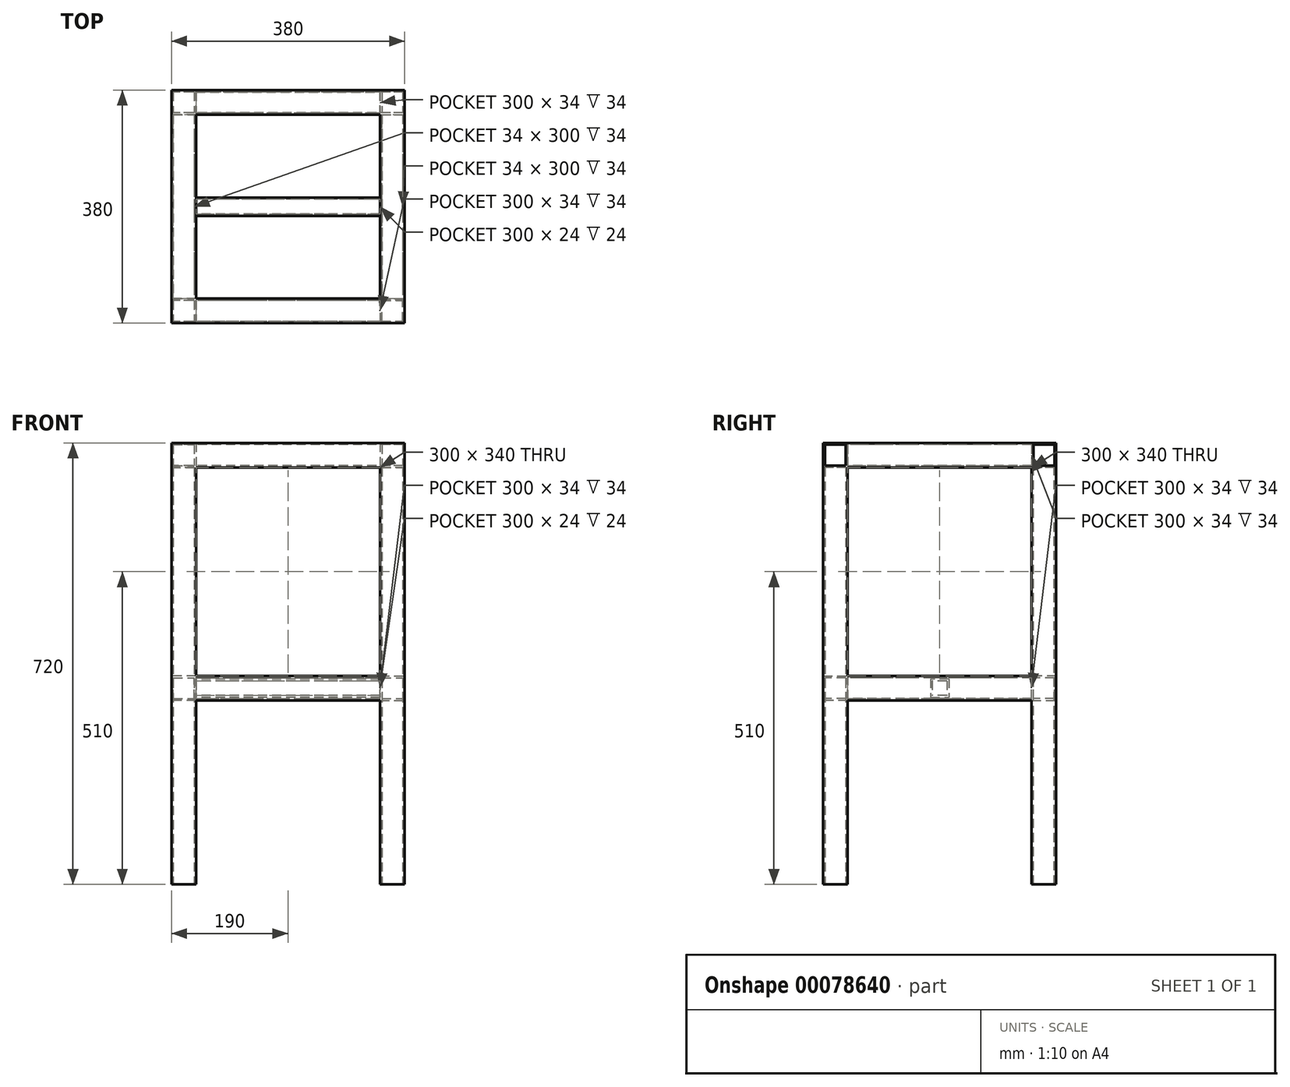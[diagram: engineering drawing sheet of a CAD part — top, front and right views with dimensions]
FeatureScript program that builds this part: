
annotation { "Feature Type Name" : "Feature", "Feature Type Description" : "" }
export const myFeature = defineFeature(function(context is Context, id is Id, definition is map)
    precondition{}
    {
        {
            var Q0;
            Q0=qCreatedBy(makeId("Top.planeOp"),FACE);
            var sketch = newSketch(context, id + "F0", { "sketchPlane" : qUnion([Q0])});
            skLineSegment(sketch, "E0.bottom", {"start": v(0, 0) * mm, "end": v(-40, 0) * mm});
            skLineSegment(sketch, "E0.top", {"start": v(0, -40) * mm, "end": v(-40, -40) * mm});
            skLineSegment(sketch, "E0.left", {"start": v(0, 0) * mm, "end": v(0, -40) * mm});
            skLineSegment(sketch, "E0.right", {"start": v(-40, 0) * mm, "end": v(-40, -40) * mm});
            skLineSegment(sketch, "E1.bottom", {"start": v(-3, -3) * mm, "end": v(-37, -3) * mm});
            skLineSegment(sketch, "E1.top", {"start": v(-3, -37) * mm, "end": v(-37, -37) * mm});
            skLineSegment(sketch, "E1.left", {"start": v(-3, -3) * mm, "end": v(-3, -37) * mm});
            skLineSegment(sketch, "E1.right", {"start": v(-37, -3) * mm, "end": v(-37, -37) * mm});
            skSolve(sketch);
        }
        {
            var Q0;
            Q0=makeQuery(id+"F0.imprint","IMPRINT",FACE,{"disambiguationData":[TD([[makeQuery(id+"F0.imprint","IMPRINT",EDGE,{"derivedFrom":sQuery(id+"F0.wireOp",EDGE,"E0.bottom")}),1.0]])]});
            extrude(context, id + "F1", {"entities" : qUnion([Q0]), "depth" : 380 * mm});
        }
        {
            var Q0;
            Q0=makeQuery(id+"F1.opExtrude","SWEPT_FACE",FACE,{"disambiguationData":[OSD([sQuery(id+"F0.wireOp",EDGE,"E0.left")])]});
            var sketch = newSketch(context, id + "F2", { "sketchPlane" : qUnion([Q0])});
            skLineSegment(sketch, "E2.bottom", {"start": v(-40, 0) * mm, "end": v(0, 0) * mm});
            skLineSegment(sketch, "E2.top", {"start": v(-40, 40) * mm, "end": v(0, 40) * mm});
            skLineSegment(sketch, "E2.left", {"start": v(-40, 0) * mm, "end": v(-40, 40) * mm});
            skLineSegment(sketch, "E2.right", {"start": v(0, 0) * mm, "end": v(0, 40) * mm});
            skLineSegment(sketch, "E3.bottom", {"start": v(-3, 37) * mm, "end": v(-37, 37) * mm});
            skLineSegment(sketch, "E3.top", {"start": v(-3, 3) * mm, "end": v(-37, 3) * mm});
            skLineSegment(sketch, "E3.left", {"start": v(-3, 37) * mm, "end": v(-3, 3) * mm});
            skLineSegment(sketch, "E3.right", {"start": v(-37, 37) * mm, "end": v(-37, 3) * mm});
            skSolve(sketch);
        }
        {
            var Q0;
            Q0 = qSketchRegion(id + "F2", true);
            extrude(context, id + "F3", {"entities" : qUnion([Q0]), "operationType" : NewBodyOperationType.ADD, "depth" : 300 * mm});
        }
        {
            var Q0;
            Q0=makeQuery(id+"F3.boolean.opBoolean","MERGE",FACE,{"derivedFrom":[makeQuery(id+"F1.opExtrude","CAP_FACE",FACE,{"disambiguationData":[OSD([sQuery(id+"F0.wireOp",EDGE,"E0.bottom"),sQuery(id+"F0.wireOp",EDGE,"E0.top"),sQuery(id+"F0.wireOp",EDGE,"E0.left"),sQuery(id+"F0.wireOp",EDGE,"E0.right"),sQuery(id+"F0.wireOp",EDGE,"E1.bottom"),sQuery(id+"F0.wireOp",EDGE,"E1.top"),sQuery(id+"F0.wireOp",EDGE,"E1.left"),sQuery(id+"F0.wireOp",EDGE,"E1.right")])],"isStart":true}),makeQuery(id+"F3.opExtrude","SWEPT_FACE",FACE,{"disambiguationData":[OSD([sQuery(id+"F2.wireOp",EDGE,"E2.bottom")])]})]});
            var sketch = newSketch(context, id + "F4", { "sketchPlane" : qUnion([Q0])});
            skLineSegment(sketch, "E4.bottom", {"start": v(300, 40) * mm, "end": v(340, 40) * mm});
            skLineSegment(sketch, "E4.top", {"start": v(300, 0) * mm, "end": v(340, 0) * mm});
            skLineSegment(sketch, "E4.left", {"start": v(300, 40) * mm, "end": v(300, 0) * mm});
            skLineSegment(sketch, "E4.right", {"start": v(340, 40) * mm, "end": v(340, 0) * mm});
            skLineSegment(sketch, "E5.bottom", {"start": v(303, 37) * mm, "end": v(337, 37) * mm});
            skLineSegment(sketch, "E5.top", {"start": v(303, 3) * mm, "end": v(337, 3) * mm});
            skLineSegment(sketch, "E5.left", {"start": v(303, 37) * mm, "end": v(303, 3) * mm});
            skLineSegment(sketch, "E5.right", {"start": v(337, 37) * mm, "end": v(337, 3) * mm});
            skSolve(sketch);
        }
        {
            var Q0;
            Q0=makeQuery(id+"F4.imprint","IMPRINT",FACE,{"disambiguationData":[TD([[makeQuery(id+"F4.imprint","IMPRINT",EDGE,{"derivedFrom":sQuery(id+"F4.wireOp",EDGE,"E4.bottom")}),-1.0]])]});
            extrude(context, id + "F5", {"entities" : qUnion([Q0]), "operationType" : NewBodyOperationType.ADD, "oppositeDirection" : true, "depth" : 380 * mm});
        }
        {
            var Q0;
            Q0=makeQuery(id+"F1.opExtrude","SWEPT_FACE",FACE,{"disambiguationData":[OSD([sQuery(id+"F0.wireOp",EDGE,"E0.right")])]});
            var sketch = newSketch(context, id + "F6", { "sketchPlane" : qUnion([Q0])});
            skLineSegment(sketch, "E6.bottom", {"start": v(40, 380) * mm, "end": v(0, 380) * mm});
            skLineSegment(sketch, "E6.top", {"start": v(40, 420) * mm, "end": v(0, 420) * mm});
            skLineSegment(sketch, "E6.left", {"start": v(40, 380) * mm, "end": v(40, 420) * mm});
            skLineSegment(sketch, "E6.right", {"start": v(0, 380) * mm, "end": v(0, 420) * mm});
            skLineSegment(sketch, "E7.bottom", {"start": v(3, 417) * mm, "end": v(37, 417) * mm});
            skLineSegment(sketch, "E7.top", {"start": v(3, 383) * mm, "end": v(37, 383) * mm});
            skLineSegment(sketch, "E7.left", {"start": v(3, 417) * mm, "end": v(3, 383) * mm});
            skLineSegment(sketch, "E7.right", {"start": v(37, 417) * mm, "end": v(37, 383) * mm});
            skSolve(sketch);
        }
        {
            var Q0;
            Q0 = qSketchRegion(id + "F6", true);
            var Q1;
            Q1=makeQuery(id+"F6.imprint","IMPRINT",FACE,{"disambiguationData":[TD([[makeQuery(id+"F6.imprint","IMPRINT",EDGE,{"derivedFrom":sQuery(id+"F6.wireOp",EDGE,"E6.bottom")}),1.0]])]});
            extrude(context, id + "F7", {"entities" : qUnion([Q0, Q1]), "operationType" : NewBodyOperationType.ADD, "oppositeDirection" : true, "depth" : 380 * mm});
        }
        {
            var Q0;
            Q0=makeQuery(id+"F7.boolean.opBoolean","MERGE",FACE,{"derivedFrom":[makeQuery(id+"F5.boolean.opBoolean","MERGE",FACE,{"derivedFrom":[makeQuery(id+"F3.boolean.opBoolean","MERGE",FACE,{"derivedFrom":[makeQuery(id+"F1.opExtrude","SWEPT_FACE",FACE,{"disambiguationData":[OSD([sQuery(id+"F0.wireOp",EDGE,"E0.bottom")])]}),makeQuery(id+"F3.opExtrude","SWEPT_FACE",FACE,{"disambiguationData":[OSD([sQuery(id+"F2.wireOp",EDGE,"E2.right")])]})]}),makeQuery(id+"F5.opExtrude","SWEPT_FACE",FACE,{"disambiguationData":[OSD([sQuery(id+"F4.wireOp",EDGE,"E4.top")])]})]}),makeQuery(id+"F7.opExtrude","SWEPT_FACE",FACE,{"disambiguationData":[OSD([sQuery(id+"F6.wireOp",EDGE,"E6.right")])]})]});
            var sketch = newSketch(context, id + "F8", { "sketchPlane" : qUnion([Q0])});
            skLineSegment(sketch, "E8.bottom", {"start": v(37, 3) * mm, "end": v(3, 3) * mm});
            skLineSegment(sketch, "E8.top", {"start": v(37, 37) * mm, "end": v(3, 37) * mm});
            skLineSegment(sketch, "E8.left", {"start": v(37, 3) * mm, "end": v(37, 37) * mm});
            skLineSegment(sketch, "E8.right", {"start": v(3, 3) * mm, "end": v(3, 37) * mm});
            skLineSegment(sketch, "E9.bottom", {"start": v(0, 40) * mm, "end": v(40, 40) * mm});
            skLineSegment(sketch, "E9.top", {"start": v(0, 0) * mm, "end": v(40, 0) * mm});
            skLineSegment(sketch, "E9.left", {"start": v(0, 40) * mm, "end": v(0, 0) * mm});
            skLineSegment(sketch, "E9.right", {"start": v(40, 40) * mm, "end": v(40, 0) * mm});
            skSolve(sketch);
        }
        {
            var Q0;
            Q0 = qSketchRegion(id + "F8", true);
            extrude(context, id + "F9", {"entities" : qUnion([Q0]), "operationType" : NewBodyOperationType.ADD, "depth" : 300 * mm});
        }
        {
            var Q0;
            {var subQ3=sQuery(id+"F4.wireOp",EDGE,"E4.top");var subQ5=sQuery(id+"F0.wireOp",EDGE,"E0.left");var subQ6=sQuery(id+"F0.wireOp",EDGE,"E0.bottom");var subQ11=sQuery(id+"F6.wireOp",EDGE,"E6.right");Q0=makeQuery(id+"F9.boolean.opBoolean","SPLIT",FACE,{"disambiguationData":[TD([makeQuery(id+"F1.opExtrude","SWEPT_FACE",FACE,{"disambiguationData":[OSD([subQ5])]})])],"derivedFrom":makeQuery(id+"F7.boolean.opBoolean","MERGE",FACE,{"derivedFrom":[makeQuery(id+"F5.boolean.opBoolean","MERGE",FACE,{"derivedFrom":[makeQuery(id+"F3.boolean.opBoolean","MERGE",FACE,{"derivedFrom":[makeQuery(id+"F1.opExtrude","SWEPT_FACE",FACE,{"disambiguationData":[OSD([subQ6])]}),makeQuery(id+"F3.opExtrude","SWEPT_FACE",FACE,{"disambiguationData":[OSD([sQuery(id+"F2.wireOp",EDGE,"E2.right")])]})]}),makeQuery(id+"F5.opExtrude","SWEPT_FACE",FACE,{"disambiguationData":[OSD([subQ3])]})]}),makeQuery(id+"F7.opExtrude","SWEPT_FACE",FACE,{"disambiguationData":[OSD([subQ11])]})]})});}
            var sketch = newSketch(context, id + "F10", { "sketchPlane" : qUnion([Q0])});
            skLineSegment(sketch, "E10.bottom", {"start": v(-300, 40) * mm, "end": v(-340, 40) * mm});
            skLineSegment(sketch, "E10.top", {"start": v(-300, 0) * mm, "end": v(-340, 0) * mm});
            skLineSegment(sketch, "E10.left", {"start": v(-300, 40) * mm, "end": v(-300, 0) * mm});
            skLineSegment(sketch, "E10.right", {"start": v(-340, 40) * mm, "end": v(-340, 0) * mm});
            skLineSegment(sketch, "E11.bottom", {"start": v(-303, 37) * mm, "end": v(-337, 37) * mm});
            skLineSegment(sketch, "E11.top", {"start": v(-303, 3) * mm, "end": v(-337, 3) * mm});
            skLineSegment(sketch, "E11.left", {"start": v(-303, 37) * mm, "end": v(-303, 3) * mm});
            skLineSegment(sketch, "E11.right", {"start": v(-337, 37) * mm, "end": v(-337, 3) * mm});
            skSolve(sketch);
        }
        {
            var Q0;
            Q0 = qSketchRegion(id + "F10", true);
            extrude(context, id + "F11", {"entities" : qUnion([Q0]), "operationType" : NewBodyOperationType.ADD, "depth" : 300 * mm});
        }
        {
            var Q0;
            {var subQ2=sQuery(id+"F4.wireOp",EDGE,"E4.top");var subQ3=makeQuery(id+"F5.opExtrude","SWEPT_FACE",FACE,{"disambiguationData":[OSD([subQ2])]});var subQ4=makeQuery(id+"F3.opExtrude","SWEPT_FACE",FACE,{"disambiguationData":[OSD([sQuery(id+"F2.wireOp",EDGE,"E2.right")])]});var subQ5=sQuery(id+"F0.wireOp",EDGE,"E0.bottom");var subQ6=makeQuery(id+"F1.opExtrude","SWEPT_FACE",FACE,{"disambiguationData":[OSD([subQ5])]});var subQ12=sQuery(id+"F6.wireOp",EDGE,"E6.right");var subQ18=sQuery(id+"F0.wireOp",EDGE,"E0.left");var subQ19=makeQuery(id+"F1.opExtrude","SWEPT_FACE",FACE,{"disambiguationData":[OSD([subQ18])]});var subQ22=sQuery(id+"F0.wireOp",EDGE,"E0.right");var subQ23=makeQuery(id+"F1.opExtrude","SWEPT_FACE",FACE,{"disambiguationData":[OSD([subQ22])]});var subQ26=makeQuery(id+"F7.opExtrude","SWEPT_FACE",FACE,{"disambiguationData":[OSD([subQ12])]});Q0=makeQuery(id+"F11.boolean.opBoolean","SPLIT",FACE,{"disambiguationData":[TD([subQ23])],"derivedFrom":makeQuery(id+"F9.boolean.opBoolean","SPLIT",FACE,{"disambiguationData":[TD([subQ19])],"derivedFrom":makeQuery(id+"F7.boolean.opBoolean","MERGE",FACE,{"derivedFrom":[makeQuery(id+"F5.boolean.opBoolean","MERGE",FACE,{"derivedFrom":[makeQuery(id+"F3.boolean.opBoolean","MERGE",FACE,{"derivedFrom":[subQ6,subQ4]}),subQ3]}),subQ26]})})});}
            var sketch = newSketch(context, id + "F12", { "sketchPlane" : qUnion([Q0])});
            skLineSegment(sketch, "E12.bottom", {"start": v(-340, 420) * mm, "end": v(-300, 420) * mm});
            skLineSegment(sketch, "E12.top", {"start": v(-340, 380) * mm, "end": v(-300, 380) * mm});
            skLineSegment(sketch, "E12.left", {"start": v(-340, 420) * mm, "end": v(-340, 380) * mm});
            skLineSegment(sketch, "E12.right", {"start": v(-300, 420) * mm, "end": v(-300, 380) * mm});
            skLineSegment(sketch, "E13.bottom", {"start": v(-337, 417) * mm, "end": v(-303, 417) * mm});
            skLineSegment(sketch, "E13.top", {"start": v(-337, 383) * mm, "end": v(-303, 383) * mm});
            skLineSegment(sketch, "E13.left", {"start": v(-337, 417) * mm, "end": v(-337, 383) * mm});
            skLineSegment(sketch, "E13.right", {"start": v(-303, 417) * mm, "end": v(-303, 383) * mm});
            skSolve(sketch);
        }
        {
            var Q0;
            Q0 = qSketchRegion(id + "F12", true);
            extrude(context, id + "F13", {"entities" : qUnion([Q0]), "operationType" : NewBodyOperationType.ADD, "depth" : 300 * mm});
        }
        {
            var Q0;
            {var subQ2=sQuery(id+"F4.wireOp",EDGE,"E4.top");var subQ3=makeQuery(id+"F5.opExtrude","SWEPT_FACE",FACE,{"disambiguationData":[OSD([subQ2])]});var subQ4=makeQuery(id+"F3.opExtrude","SWEPT_FACE",FACE,{"disambiguationData":[OSD([sQuery(id+"F2.wireOp",EDGE,"E2.right")])]});var subQ5=sQuery(id+"F0.wireOp",EDGE,"E0.bottom");var subQ6=makeQuery(id+"F1.opExtrude","SWEPT_FACE",FACE,{"disambiguationData":[OSD([subQ5])]});var subQ12=sQuery(id+"F6.wireOp",EDGE,"E6.right");var subQ18=sQuery(id+"F0.wireOp",EDGE,"E0.left");var subQ19=makeQuery(id+"F1.opExtrude","SWEPT_FACE",FACE,{"disambiguationData":[OSD([subQ18])]});var subQ22=sQuery(id+"F0.wireOp",EDGE,"E0.right");var subQ23=makeQuery(id+"F1.opExtrude","SWEPT_FACE",FACE,{"disambiguationData":[OSD([subQ22])]});var subQ26=makeQuery(id+"F7.opExtrude","SWEPT_FACE",FACE,{"disambiguationData":[OSD([subQ12])]});Q0=makeQuery(id+"F11.boolean.opBoolean","SPLIT",FACE,{"disambiguationData":[TD([subQ23])],"derivedFrom":makeQuery(id+"F9.boolean.opBoolean","SPLIT",FACE,{"disambiguationData":[TD([subQ19])],"derivedFrom":makeQuery(id+"F7.boolean.opBoolean","MERGE",FACE,{"derivedFrom":[makeQuery(id+"F5.boolean.opBoolean","MERGE",FACE,{"derivedFrom":[makeQuery(id+"F3.boolean.opBoolean","MERGE",FACE,{"derivedFrom":[subQ6,subQ4]}),subQ3]}),subQ26]})})});}
            var sketch = newSketch(context, id + "F14", { "sketchPlane" : qUnion([Q0])});
            skLineSegment(sketch, "E14.bottom", {"start": v(40, 420) * mm, "end": v(0, 420) * mm});
            skLineSegment(sketch, "E14.top", {"start": v(40, 380) * mm, "end": v(0, 380) * mm});
            skLineSegment(sketch, "E14.left", {"start": v(40, 420) * mm, "end": v(40, 380) * mm});
            skLineSegment(sketch, "E14.right", {"start": v(0, 420) * mm, "end": v(0, 380) * mm});
            skLineSegment(sketch, "E15.bottom", {"start": v(37, 417) * mm, "end": v(3, 417) * mm});
            skLineSegment(sketch, "E15.top", {"start": v(37, 383) * mm, "end": v(3, 383) * mm});
            skLineSegment(sketch, "E15.left", {"start": v(37, 417) * mm, "end": v(37, 383) * mm});
            skLineSegment(sketch, "E15.right", {"start": v(3, 417) * mm, "end": v(3, 383) * mm});
            skSolve(sketch);
        }
        {
            var Q0;
            Q0 = qSketchRegion(id + "F14", true);
            extrude(context, id + "F15", {"entities" : qUnion([Q0]), "operationType" : NewBodyOperationType.ADD, "depth" : 300 * mm});
        }
        {
            var Q0;
            Q0=makeQuery(id+"F15.boolean.opBoolean","MERGE",FACE,{"derivedFrom":[makeQuery(id+"F9.boolean.opBoolean","MERGE",FACE,{"derivedFrom":[makeQuery(id+"F7.boolean.opBoolean","MERGE",FACE,{"derivedFrom":[makeQuery(id+"F1.opExtrude","SWEPT_FACE",FACE,{"disambiguationData":[OSD([sQuery(id+"F0.wireOp",EDGE,"E0.right")])]}),makeQuery(id+"F7.opExtrude","CAP_FACE",FACE,{"disambiguationData":[OSD([sQuery(id+"F6.wireOp",EDGE,"E6.bottom"),sQuery(id+"F6.wireOp",EDGE,"E6.top"),sQuery(id+"F6.wireOp",EDGE,"E6.left"),sQuery(id+"F6.wireOp",EDGE,"E6.right"),sQuery(id+"F6.wireOp",EDGE,"E7.bottom"),sQuery(id+"F6.wireOp",EDGE,"E7.top"),sQuery(id+"F6.wireOp",EDGE,"E7.left"),sQuery(id+"F6.wireOp",EDGE,"E7.right")])],"isStart":true})]}),makeQuery(id+"F9.opExtrude","SWEPT_FACE",FACE,{"disambiguationData":[OSD([sQuery(id+"F8.wireOp",EDGE,"E9.right")])]})]}),makeQuery(id+"F15.opExtrude","SWEPT_FACE",FACE,{"disambiguationData":[OSD([sQuery(id+"F14.wireOp",EDGE,"E14.left")])]})]});
            var sketch = newSketch(context, id + "F16", { "sketchPlane" : qUnion([Q0])});
            skLineSegment(sketch, "E16.bottom", {"start": v(-300, 420) * mm, "end": v(-340, 420) * mm});
            skLineSegment(sketch, "E16.top", {"start": v(-300, 380) * mm, "end": v(-340, 380) * mm});
            skLineSegment(sketch, "E16.left", {"start": v(-300, 420) * mm, "end": v(-300, 380) * mm});
            skLineSegment(sketch, "E16.right", {"start": v(-340, 420) * mm, "end": v(-340, 380) * mm});
            skLineSegment(sketch, "E17.bottom", {"start": v(-303, 417) * mm, "end": v(-337, 417) * mm});
            skLineSegment(sketch, "E17.top", {"start": v(-303, 383) * mm, "end": v(-337, 383) * mm});
            skLineSegment(sketch, "E17.left", {"start": v(-303, 417) * mm, "end": v(-303, 383) * mm});
            skLineSegment(sketch, "E17.right", {"start": v(-337, 417) * mm, "end": v(-337, 383) * mm});
            skSolve(sketch);
        }
        {
            var Q0;
            Q0 = qSketchRegion(id + "F16", true);
            extrude(context, id + "F17", {"entities" : qUnion([Q0]), "operationType" : NewBodyOperationType.ADD, "oppositeDirection" : true, "depth" : 380 * mm});
        }
        {
            var Q0;
            Q0=makeQuery(id+"F17.boolean.opBoolean","MERGE",FACE,{"derivedFrom":[makeQuery(id+"F13.opExtrude","SWEPT_FACE",FACE,{"disambiguationData":[OSD([sQuery(id+"F12.wireOp",EDGE,"E12.top")])]}),makeQuery(id+"F15.opExtrude","SWEPT_FACE",FACE,{"disambiguationData":[OSD([sQuery(id+"F14.wireOp",EDGE,"E14.top")])]}),makeQuery(id+"F17.opExtrude","SWEPT_FACE",FACE,{"disambiguationData":[OSD([sQuery(id+"F16.wireOp",EDGE,"E16.top")])]})]});
            var sketch = newSketch(context, id + "F18", { "sketchPlane" : qUnion([Q0])});
            skLineSegment(sketch, "E18.bottom", {"start": v(340, -340) * mm, "end": v(300, -340) * mm});
            skLineSegment(sketch, "E18.top", {"start": v(340, -300) * mm, "end": v(300, -300) * mm});
            skLineSegment(sketch, "E18.left", {"start": v(340, -340) * mm, "end": v(340, -300) * mm});
            skLineSegment(sketch, "E18.right", {"start": v(300, -340) * mm, "end": v(300, -300) * mm});
            skLineSegment(sketch, "E19.bottom", {"start": v(337, -336.7) * mm, "end": v(303, -336.7) * mm});
            skLineSegment(sketch, "E19.top", {"start": v(337, -303) * mm, "end": v(303, -303) * mm});
            skLineSegment(sketch, "E19.left", {"start": v(337, -336.7) * mm, "end": v(337, -303) * mm});
            skLineSegment(sketch, "E19.right", {"start": v(303, -336.7) * mm, "end": v(303, -303) * mm});
            skSolve(sketch);
        }
        {
            var Q0;
            Q0 = qSketchRegion(id + "F18", true);
            extrude(context, id + "F19", {"entities" : qUnion([Q0]), "operationType" : NewBodyOperationType.ADD, "depth" : 380 * mm});
        }
        {
            var Q0;
            {var subQ2=sQuery(id+"F16.wireOp",EDGE,"E16.top");var subQ3=makeQuery(id+"F17.opExtrude","SWEPT_FACE",FACE,{"disambiguationData":[OSD([subQ2])]});var subQ5=makeQuery(id+"F13.opExtrude","SWEPT_FACE",FACE,{"disambiguationData":[OSD([sQuery(id+"F12.wireOp",EDGE,"E12.top")])]});var subQ6=makeQuery(id+"F15.opExtrude","SWEPT_FACE",FACE,{"disambiguationData":[OSD([sQuery(id+"F14.wireOp",EDGE,"E14.top")])]});Q0=makeQuery(id+"F19.boolean.opBoolean","SPLIT",FACE,{"disambiguationData":[TD([makeQuery(id+"F1.opExtrude","SWEPT_FACE",FACE,{"disambiguationData":[OSD([sQuery(id+"F0.wireOp",EDGE,"E0.left")])]})])],"derivedFrom":makeQuery(id+"F17.boolean.opBoolean","MERGE",FACE,{"derivedFrom":[subQ5,subQ6,subQ3]})});}
            var sketch = newSketch(context, id + "F20", { "sketchPlane" : qUnion([Q0])});
            skLineSegment(sketch, "E20.bottom", {"start": v(-40, -340) * mm, "end": v(0, -340) * mm});
            skLineSegment(sketch, "E20.top", {"start": v(-40, -300) * mm, "end": v(0, -300) * mm});
            skLineSegment(sketch, "E20.left", {"start": v(-40, -340) * mm, "end": v(-40, -300) * mm});
            skLineSegment(sketch, "E20.right", {"start": v(0, -340) * mm, "end": v(0, -300) * mm});
            skLineSegment(sketch, "E21.bottom", {"start": v(-3, -337) * mm, "end": v(-37, -337) * mm});
            skLineSegment(sketch, "E21.top", {"start": v(-3, -303) * mm, "end": v(-37, -303) * mm});
            skLineSegment(sketch, "E21.left", {"start": v(-3, -337) * mm, "end": v(-3, -303) * mm});
            skLineSegment(sketch, "E21.right", {"start": v(-37, -337) * mm, "end": v(-37, -303) * mm});
            skSolve(sketch);
        }
        {
            var Q0;
            Q0 = qSketchRegion(id + "F20", true);
            extrude(context, id + "F21", {"entities" : qUnion([Q0]), "operationType" : NewBodyOperationType.ADD, "depth" : 380 * mm});
        }
        {
            var Q0;
            Q0=makeQuery(id+"F20.imprint","IMPRINT",FACE,{"disambiguationData":[TD([[makeQuery(id+"F20.imprint","IMPRINT",EDGE,{"derivedFrom":sQuery(id+"F20.wireOp",EDGE,"E20.bottom")}),-1.0]])]});
            extrude(context, id + "F22", {"entities" : qUnion([Q0]), "operationType" : NewBodyOperationType.ADD, "depth" : 25 * mm});
        }
        {
            var Q0;
            Q0=makeQuery(id+"F19.boolean.opBoolean","MERGE",FACE,{"derivedFrom":[makeQuery(id+"F11.opExtrude","SWEPT_FACE",FACE,{"disambiguationData":[OSD([sQuery(id+"F10.wireOp",EDGE,"E10.left")])]}),makeQuery(id+"F19.opExtrude","SWEPT_FACE",FACE,{"disambiguationData":[OSD([sQuery(id+"F18.wireOp",EDGE,"E18.right")])]})]});
            var sketch = newSketch(context, id + "F23", { "sketchPlane" : qUnion([Q0])});
            skLineSegment(sketch, "E22.bottom", {"start": v(-340, 0) * mm, "end": v(-300, 0) * mm});
            skLineSegment(sketch, "E22.top", {"start": v(-340, 40) * mm, "end": v(-300, 40) * mm});
            skLineSegment(sketch, "E22.left", {"start": v(-340, 0) * mm, "end": v(-340, 40) * mm});
            skLineSegment(sketch, "E22.right", {"start": v(-300, 0) * mm, "end": v(-300, 40) * mm});
            skLineSegment(sketch, "E23.bottom", {"start": v(-337, 3) * mm, "end": v(-303, 3) * mm});
            skLineSegment(sketch, "E23.top", {"start": v(-337, 37) * mm, "end": v(-303, 37) * mm});
            skLineSegment(sketch, "E23.left", {"start": v(-337, 3) * mm, "end": v(-337, 37) * mm});
            skLineSegment(sketch, "E23.right", {"start": v(-303, 3) * mm, "end": v(-303, 37) * mm});
            skSolve(sketch);
        }
        {
            var Q0;
            Q0 = qSketchRegion(id + "F23", true);
            extrude(context, id + "F24", {"entities" : qUnion([Q0]), "operationType" : NewBodyOperationType.ADD, "depth" : 300 * mm});
        }
        {
            var Q0;
            Q0=makeQuery(id+"F24.boolean.opBoolean","MERGE",FACE,{"derivedFrom":[makeQuery(id+"F21.boolean.opBoolean","MERGE",FACE,{"derivedFrom":[makeQuery(id+"F19.boolean.opBoolean","MERGE",FACE,{"derivedFrom":[makeQuery(id+"F11.boolean.opBoolean","MERGE",FACE,{"derivedFrom":[makeQuery(id+"F9.boolean.opBoolean","MERGE",FACE,{"derivedFrom":[makeQuery(id+"F5.boolean.opBoolean","MERGE",FACE,{"derivedFrom":[makeQuery(id+"F3.boolean.opBoolean","MERGE",FACE,{"derivedFrom":[makeQuery(id+"F1.opExtrude","CAP_FACE",FACE,{"disambiguationData":[OSD([sQuery(id+"F0.wireOp",EDGE,"E0.bottom"),sQuery(id+"F0.wireOp",EDGE,"E0.top"),sQuery(id+"F0.wireOp",EDGE,"E0.left"),sQuery(id+"F0.wireOp",EDGE,"E0.right"),sQuery(id+"F0.wireOp",EDGE,"E1.bottom"),sQuery(id+"F0.wireOp",EDGE,"E1.top"),sQuery(id+"F0.wireOp",EDGE,"E1.left"),sQuery(id+"F0.wireOp",EDGE,"E1.right")])],"isStart":true}),makeQuery(id+"F3.opExtrude","SWEPT_FACE",FACE,{"disambiguationData":[OSD([sQuery(id+"F2.wireOp",EDGE,"E2.bottom")])]})]}),makeQuery(id+"F5.opExtrude","CAP_FACE",FACE,{"disambiguationData":[OSD([sQuery(id+"F4.wireOp",EDGE,"E4.bottom"),sQuery(id+"F4.wireOp",EDGE,"E4.top"),sQuery(id+"F4.wireOp",EDGE,"E4.left"),sQuery(id+"F4.wireOp",EDGE,"E4.right"),sQuery(id+"F4.wireOp",EDGE,"E5.bottom"),sQuery(id+"F4.wireOp",EDGE,"E5.top"),sQuery(id+"F4.wireOp",EDGE,"E5.left"),sQuery(id+"F4.wireOp",EDGE,"E5.right")])],"isStart":true})]}),makeQuery(id+"F9.opExtrude","SWEPT_FACE",FACE,{"disambiguationData":[OSD([sQuery(id+"F8.wireOp",EDGE,"E9.top")])]})]}),makeQuery(id+"F11.opExtrude","SWEPT_FACE",FACE,{"disambiguationData":[OSD([sQuery(id+"F10.wireOp",EDGE,"E10.top")])]})]}),makeQuery(id+"F19.opExtrude","CAP_FACE",FACE,{"disambiguationData":[OSD([sQuery(id+"F18.wireOp",EDGE,"E18.bottom"),sQuery(id+"F18.wireOp",EDGE,"E18.top"),sQuery(id+"F18.wireOp",EDGE,"E18.left"),sQuery(id+"F18.wireOp",EDGE,"E18.right"),sQuery(id+"F18.wireOp",EDGE,"E19.bottom"),sQuery(id+"F18.wireOp",EDGE,"E19.top"),sQuery(id+"F18.wireOp",EDGE,"E19.left"),sQuery(id+"F18.wireOp",EDGE,"E19.right")])],"isStart":false})]}),makeQuery(id+"F21.opExtrude","CAP_FACE",FACE,{"disambiguationData":[OSD([sQuery(id+"F20.wireOp",EDGE,"E20.bottom"),sQuery(id+"F20.wireOp",EDGE,"E20.top"),sQuery(id+"F20.wireOp",EDGE,"E20.left"),sQuery(id+"F20.wireOp",EDGE,"E20.right"),sQuery(id+"F20.wireOp",EDGE,"E21.bottom"),sQuery(id+"F20.wireOp",EDGE,"E21.top"),sQuery(id+"F20.wireOp",EDGE,"E21.left"),sQuery(id+"F20.wireOp",EDGE,"E21.right")])],"isStart":false})]}),makeQuery(id+"F24.opExtrude","SWEPT_FACE",FACE,{"disambiguationData":[OSD([sQuery(id+"F23.wireOp",EDGE,"E22.bottom")])]})]});
            var sketch = newSketch(context, id + "F25", { "sketchPlane" : qUnion([Q0])});
            skLineSegment(sketch, "E24", {"start": v(300, -300) * mm, "end": v(340, -300) * mm});
            skLineSegment(sketch, "E25", {"start": v(300, -300) * mm, "end": v(300, -340) * mm});
            skLineSegment(sketch, "E26", {"start": v(0, -300) * mm, "end": v(-40, -300) * mm});
            skLineSegment(sketch, "E27", {"start": v(0, -300) * mm, "end": v(0, -340) * mm});
            skLineSegment(sketch, "E28", {"start": v(300, 0) * mm, "end": v(340, 0) * mm});
            skLineSegment(sketch, "E29", {"start": v(300, 0) * mm, "end": v(300, 40) * mm});
            skLineSegment(sketch, "E30", {"start": v(0, 0) * mm, "end": v(-40, 0) * mm});
            skLineSegment(sketch, "E31", {"start": v(0, 0) * mm, "end": v(0, 40) * mm});
            skSolve(sketch);
        }
        {
            var Q0;
            {var subQ1=sQuery(id+"F25.wireOp",EDGE,"E30");Q0=makeQuery(id+"F25.imprint","IMPRINT",FACE,{"disambiguationData":[TD([[makeQuery(id+"F25.imprint","IMPRINT",EDGE,{"derivedFrom":subQ1}),-1.0]])]});}
            extrude(context, id + "F26", {"entities" : qUnion([Q0]), "operationType" : NewBodyOperationType.ADD, "depth" : 300 * mm});
        }
        {
            var Q0;
            Q0=makeQuery(id+"F24.boolean.opBoolean","MERGE",FACE,{"derivedFrom":[makeQuery(id+"F21.boolean.opBoolean","MERGE",FACE,{"derivedFrom":[makeQuery(id+"F19.boolean.opBoolean","MERGE",FACE,{"derivedFrom":[makeQuery(id+"F11.boolean.opBoolean","MERGE",FACE,{"derivedFrom":[makeQuery(id+"F9.boolean.opBoolean","MERGE",FACE,{"derivedFrom":[makeQuery(id+"F5.boolean.opBoolean","MERGE",FACE,{"derivedFrom":[makeQuery(id+"F3.boolean.opBoolean","MERGE",FACE,{"derivedFrom":[makeQuery(id+"F1.opExtrude","CAP_FACE",FACE,{"disambiguationData":[OSD([sQuery(id+"F0.wireOp",EDGE,"E0.bottom"),sQuery(id+"F0.wireOp",EDGE,"E0.top"),sQuery(id+"F0.wireOp",EDGE,"E0.left"),sQuery(id+"F0.wireOp",EDGE,"E0.right"),sQuery(id+"F0.wireOp",EDGE,"E1.bottom"),sQuery(id+"F0.wireOp",EDGE,"E1.top"),sQuery(id+"F0.wireOp",EDGE,"E1.left"),sQuery(id+"F0.wireOp",EDGE,"E1.right")])],"isStart":true}),makeQuery(id+"F3.opExtrude","SWEPT_FACE",FACE,{"disambiguationData":[OSD([sQuery(id+"F2.wireOp",EDGE,"E2.bottom")])]})]}),makeQuery(id+"F5.opExtrude","CAP_FACE",FACE,{"disambiguationData":[OSD([sQuery(id+"F4.wireOp",EDGE,"E4.bottom"),sQuery(id+"F4.wireOp",EDGE,"E4.top"),sQuery(id+"F4.wireOp",EDGE,"E4.left"),sQuery(id+"F4.wireOp",EDGE,"E4.right"),sQuery(id+"F4.wireOp",EDGE,"E5.bottom"),sQuery(id+"F4.wireOp",EDGE,"E5.top"),sQuery(id+"F4.wireOp",EDGE,"E5.left"),sQuery(id+"F4.wireOp",EDGE,"E5.right")])],"isStart":true})]}),makeQuery(id+"F9.opExtrude","SWEPT_FACE",FACE,{"disambiguationData":[OSD([sQuery(id+"F8.wireOp",EDGE,"E9.top")])]})]}),makeQuery(id+"F11.opExtrude","SWEPT_FACE",FACE,{"disambiguationData":[OSD([sQuery(id+"F10.wireOp",EDGE,"E10.top")])]})]}),makeQuery(id+"F19.opExtrude","CAP_FACE",FACE,{"disambiguationData":[OSD([sQuery(id+"F18.wireOp",EDGE,"E18.bottom"),sQuery(id+"F18.wireOp",EDGE,"E18.top"),sQuery(id+"F18.wireOp",EDGE,"E18.left"),sQuery(id+"F18.wireOp",EDGE,"E18.right"),sQuery(id+"F18.wireOp",EDGE,"E19.bottom"),sQuery(id+"F18.wireOp",EDGE,"E19.top"),sQuery(id+"F18.wireOp",EDGE,"E19.left"),sQuery(id+"F18.wireOp",EDGE,"E19.right")])],"isStart":false})]}),makeQuery(id+"F21.opExtrude","CAP_FACE",FACE,{"disambiguationData":[OSD([sQuery(id+"F20.wireOp",EDGE,"E20.bottom"),sQuery(id+"F20.wireOp",EDGE,"E20.top"),sQuery(id+"F20.wireOp",EDGE,"E20.left"),sQuery(id+"F20.wireOp",EDGE,"E20.right"),sQuery(id+"F20.wireOp",EDGE,"E21.bottom"),sQuery(id+"F20.wireOp",EDGE,"E21.top"),sQuery(id+"F20.wireOp",EDGE,"E21.left"),sQuery(id+"F20.wireOp",EDGE,"E21.right")])],"isStart":false})]}),makeQuery(id+"F24.opExtrude","SWEPT_FACE",FACE,{"disambiguationData":[OSD([sQuery(id+"F23.wireOp",EDGE,"E22.bottom")])]})]});
            var sketch = newSketch(context, id + "F27", { "sketchPlane" : qUnion([Q0])});
            skLineSegment(sketch, "E32.bottom", {"start": v(300, 0) * mm, "end": v(340, 0) * mm});
            skLineSegment(sketch, "E32.top", {"start": v(300, 40) * mm, "end": v(340, 40) * mm});
            skLineSegment(sketch, "E32.left", {"start": v(300, 0) * mm, "end": v(300, 40) * mm});
            skLineSegment(sketch, "E32.right", {"start": v(340, 0) * mm, "end": v(340, 40) * mm});
            skSolve(sketch);
        }
        {
            var Q0;
            Q0=makeQuery(id+"F27.imprint","IMPRINT",FACE,{"disambiguationData":[TD([[makeQuery(id+"F27.imprint","IMPRINT",EDGE,{"derivedFrom":sQuery(id+"F27.wireOp",EDGE,"E32.bottom")}),1.0]])]});
            extrude(context, id + "F28", {"entities" : qUnion([Q0]), "operationType" : NewBodyOperationType.ADD, "depth" : 300 * mm});
        }
        {
            var Q0;
            {var subQ0=makeQuery(id+"F24.opExtrude","SWEPT_FACE",FACE,{"disambiguationData":[OSD([sQuery(id+"F23.wireOp",EDGE,"E22.bottom")])]});var subQ1=sQuery(id+"F20.wireOp",EDGE,"E21.bottom");var subQ2=sQuery(id+"F8.wireOp",EDGE,"E9.top");var subQ3=makeQuery(id+"F9.opExtrude","SWEPT_FACE",FACE,{"disambiguationData":[OSD([subQ2])]});var subQ4=sQuery(id+"F20.wireOp",EDGE,"E21.right");var subQ5=sQuery(id+"F20.wireOp",EDGE,"E20.right");var subQ6=sQuery(id+"F20.wireOp",EDGE,"E21.left");var subQ7=sQuery(id+"F20.wireOp",EDGE,"E21.top");var subQ8=sQuery(id+"F20.wireOp",EDGE,"E20.left");var subQ9=sQuery(id+"F20.wireOp",EDGE,"E20.bottom");var subQ10=makeQuery(id+"F21.opExtrude","CAP_FACE",FACE,{"disambiguationData":[OSD([subQ9,sQuery(id+"F20.wireOp",EDGE,"E20.top"),subQ8,subQ5,subQ1,subQ7,subQ6,subQ4])],"isStart":false});var subQ11=sQuery(id+"F18.wireOp",EDGE,"E19.right");var subQ12=sQuery(id+"F0.wireOp",EDGE,"E0.right");var subQ13=sQuery(id+"F18.wireOp",EDGE,"E19.left");var subQ14=sQuery(id+"F18.wireOp",EDGE,"E19.top");var subQ15=sQuery(id+"F18.wireOp",EDGE,"E19.bottom");var subQ16=sQuery(id+"F18.wireOp",EDGE,"E18.right");var subQ17=sQuery(id+"F0.wireOp",EDGE,"E0.bottom");var subQ18=makeQuery(id+"F1.opExtrude","CAP_FACE",FACE,{"disambiguationData":[OSD([subQ17,sQuery(id+"F0.wireOp",EDGE,"E0.top"),sQuery(id+"F0.wireOp",EDGE,"E0.left"),subQ12,sQuery(id+"F0.wireOp",EDGE,"E1.bottom"),sQuery(id+"F0.wireOp",EDGE,"E1.top"),sQuery(id+"F0.wireOp",EDGE,"E1.left"),sQuery(id+"F0.wireOp",EDGE,"E1.right")])],"isStart":true});var subQ27=sQuery(id+"F18.wireOp",EDGE,"E18.bottom");var subQ28=sQuery(id+"F4.wireOp",EDGE,"E4.top");var subQ29=sQuery(id+"F4.wireOp",EDGE,"E4.right");var subQ30=sQuery(id+"F18.wireOp",EDGE,"E18.left");var subQ39=makeQuery(id+"F19.opExtrude","CAP_FACE",FACE,{"disambiguationData":[OSD([subQ27,sQuery(id+"F18.wireOp",EDGE,"E18.top"),subQ30,subQ16,subQ15,subQ14,subQ13,subQ11])],"isStart":false});var subQ40=makeQuery(id+"F5.opExtrude","CAP_FACE",FACE,{"disambiguationData":[OSD([sQuery(id+"F4.wireOp",EDGE,"E4.bottom"),subQ28,sQuery(id+"F4.wireOp",EDGE,"E4.left"),subQ29,sQuery(id+"F4.wireOp",EDGE,"E5.bottom"),sQuery(id+"F4.wireOp",EDGE,"E5.top"),sQuery(id+"F4.wireOp",EDGE,"E5.left"),sQuery(id+"F4.wireOp",EDGE,"E5.right")])],"isStart":true});var subQ42=makeQuery(id+"F3.opExtrude","SWEPT_FACE",FACE,{"disambiguationData":[OSD([sQuery(id+"F2.wireOp",EDGE,"E2.bottom")])]});var subQ43=makeQuery(id+"F11.opExtrude","SWEPT_FACE",FACE,{"disambiguationData":[OSD([sQuery(id+"F10.wireOp",EDGE,"E10.top")])]});Q0=makeQuery(id+"F28.boolean.opBoolean","SPLIT",FACE,{"disambiguationData":[TD([makeQuery(id+"F1.opExtrude","SWEPT_FACE",FACE,{"disambiguationData":[OSD([subQ12])]})])],"derivedFrom":makeQuery(id+"F24.boolean.opBoolean","MERGE",FACE,{"derivedFrom":[makeQuery(id+"F21.boolean.opBoolean","MERGE",FACE,{"derivedFrom":[makeQuery(id+"F19.boolean.opBoolean","MERGE",FACE,{"derivedFrom":[makeQuery(id+"F11.boolean.opBoolean","MERGE",FACE,{"derivedFrom":[makeQuery(id+"F9.boolean.opBoolean","MERGE",FACE,{"derivedFrom":[makeQuery(id+"F5.boolean.opBoolean","MERGE",FACE,{"derivedFrom":[makeQuery(id+"F3.boolean.opBoolean","MERGE",FACE,{"derivedFrom":[subQ18,subQ42]}),subQ40]}),subQ3]}),subQ43]}),subQ39]}),subQ10]}),subQ0]})});}
            var sketch = newSketch(context, id + "F29", { "sketchPlane" : qUnion([Q0])});
            skLineSegment(sketch, "E33.bottom", {"start": v(300, -300) * mm, "end": v(340, -300) * mm});
            skLineSegment(sketch, "E33.top", {"start": v(300, -340) * mm, "end": v(340, -340) * mm});
            skLineSegment(sketch, "E33.left", {"start": v(300, -300) * mm, "end": v(300, -340) * mm});
            skLineSegment(sketch, "E33.right", {"start": v(340, -300) * mm, "end": v(340, -340) * mm});
            skSolve(sketch);
        }
        {
            var Q0;
            Q0=makeQuery(id+"F29.imprint","IMPRINT",FACE,{"disambiguationData":[TD([[makeQuery(id+"F29.imprint","IMPRINT",EDGE,{"derivedFrom":sQuery(id+"F29.wireOp",EDGE,"E33.bottom")}),-1.0]])]});
            var sketch = newSketch(context, id + "F30", { "sketchPlane" : qUnion([Q0])});
            skSolve(sketch);
        }
        {
            var Q0;
            Q0 = qSketchRegion(id + "F30", true);
            var Q1;
            Q1=makeQuery(id+"F29.imprint","IMPRINT",FACE,{"disambiguationData":[TD([[makeQuery(id+"F29.imprint","IMPRINT",EDGE,{"derivedFrom":sQuery(id+"F29.wireOp",EDGE,"E33.bottom")}),-1.0]])]});
            extrude(context, id + "F31", {"entities" : qUnion([Q0, Q1]), "operationType" : NewBodyOperationType.ADD, "depth" : 300 * mm});
        }
        {
            var Q0;
            {var subQ0=sQuery(id+"F20.wireOp",EDGE,"E20.bottom");var subQ2=sQuery(id+"F18.wireOp",EDGE,"E18.bottom");var subQ14=makeQuery(id+"F11.opExtrude","SWEPT_FACE",FACE,{"disambiguationData":[OSD([sQuery(id+"F10.wireOp",EDGE,"E10.top")])]});var subQ18=makeQuery(id+"F3.opExtrude","SWEPT_FACE",FACE,{"disambiguationData":[OSD([sQuery(id+"F2.wireOp",EDGE,"E2.bottom")])]});var subQ19=sQuery(id+"F20.wireOp",EDGE,"E20.left");var subQ21=sQuery(id+"F8.wireOp",EDGE,"E9.top");var subQ22=sQuery(id+"F0.wireOp",EDGE,"E0.right");var subQ24=makeQuery(id+"F1.opExtrude","SWEPT_FACE",FACE,{"disambiguationData":[OSD([subQ22])]});var subQ26=sQuery(id+"F20.wireOp",EDGE,"E21.left");var subQ28=sQuery(id+"F0.wireOp",EDGE,"E0.bottom");var subQ29=makeQuery(id+"F1.opExtrude","CAP_FACE",FACE,{"disambiguationData":[OSD([subQ28,sQuery(id+"F0.wireOp",EDGE,"E0.top"),sQuery(id+"F0.wireOp",EDGE,"E0.left"),subQ22,sQuery(id+"F0.wireOp",EDGE,"E1.bottom"),sQuery(id+"F0.wireOp",EDGE,"E1.top"),sQuery(id+"F0.wireOp",EDGE,"E1.left"),sQuery(id+"F0.wireOp",EDGE,"E1.right")])],"isStart":true});var subQ32=sQuery(id+"F18.wireOp",EDGE,"E18.right");var subQ37=sQuery(id+"F18.wireOp",EDGE,"E19.right");var subQ38=sQuery(id+"F18.wireOp",EDGE,"E19.left");var subQ39=sQuery(id+"F18.wireOp",EDGE,"E19.top");var subQ40=sQuery(id+"F18.wireOp",EDGE,"E19.bottom");var subQ41=sQuery(id+"F18.wireOp",EDGE,"E18.left");var subQ42=makeQuery(id+"F19.opExtrude","CAP_FACE",FACE,{"disambiguationData":[OSD([subQ2,sQuery(id+"F18.wireOp",EDGE,"E18.top"),subQ41,subQ32,subQ40,subQ39,subQ38,subQ37])],"isStart":false});var subQ43=sQuery(id+"F4.wireOp",EDGE,"E4.right");var subQ44=sQuery(id+"F4.wireOp",EDGE,"E4.top");var subQ45=makeQuery(id+"F5.opExtrude","CAP_FACE",FACE,{"disambiguationData":[OSD([sQuery(id+"F4.wireOp",EDGE,"E4.bottom"),subQ44,sQuery(id+"F4.wireOp",EDGE,"E4.left"),subQ43,sQuery(id+"F4.wireOp",EDGE,"E5.bottom"),sQuery(id+"F4.wireOp",EDGE,"E5.top"),sQuery(id+"F4.wireOp",EDGE,"E5.left"),sQuery(id+"F4.wireOp",EDGE,"E5.right")])],"isStart":true});var subQ48=sQuery(id+"F20.wireOp",EDGE,"E21.top");var subQ58=sQuery(id+"F20.wireOp",EDGE,"E21.right");var subQ59=sQuery(id+"F20.wireOp",EDGE,"E21.bottom");var subQ60=sQuery(id+"F20.wireOp",EDGE,"E20.right");var subQ61=makeQuery(id+"F21.opExtrude","CAP_FACE",FACE,{"disambiguationData":[OSD([subQ0,sQuery(id+"F20.wireOp",EDGE,"E20.top"),subQ19,subQ60,subQ59,subQ48,subQ26,subQ58])],"isStart":false});var subQ62=makeQuery(id+"F9.opExtrude","SWEPT_FACE",FACE,{"disambiguationData":[OSD([subQ21])]});var subQ66=makeQuery(id+"F24.opExtrude","SWEPT_FACE",FACE,{"disambiguationData":[OSD([sQuery(id+"F23.wireOp",EDGE,"E22.bottom")])]});Q0=makeQuery(id+"F31.boolean.opBoolean","SPLIT",FACE,{"disambiguationData":[TD([subQ24])],"derivedFrom":makeQuery(id+"F28.boolean.opBoolean","SPLIT",FACE,{"disambiguationData":[TD([subQ24])],"derivedFrom":makeQuery(id+"F24.boolean.opBoolean","MERGE",FACE,{"derivedFrom":[makeQuery(id+"F21.boolean.opBoolean","MERGE",FACE,{"derivedFrom":[makeQuery(id+"F19.boolean.opBoolean","MERGE",FACE,{"derivedFrom":[makeQuery(id+"F11.boolean.opBoolean","MERGE",FACE,{"derivedFrom":[makeQuery(id+"F9.boolean.opBoolean","MERGE",FACE,{"derivedFrom":[makeQuery(id+"F5.boolean.opBoolean","MERGE",FACE,{"derivedFrom":[makeQuery(id+"F3.boolean.opBoolean","MERGE",FACE,{"derivedFrom":[subQ29,subQ18]}),subQ45]}),subQ62]}),subQ14]}),subQ42]}),subQ61]}),subQ66]})})});}
            var sketch = newSketch(context, id + "F32", { "sketchPlane" : qUnion([Q0])});
            skLineSegment(sketch, "E34.bottom", {"start": v(0, -300) * mm, "end": v(-40, -300) * mm});
            skLineSegment(sketch, "E34.top", {"start": v(0, -340) * mm, "end": v(-40, -340) * mm});
            skLineSegment(sketch, "E34.left", {"start": v(0, -300) * mm, "end": v(0, -340) * mm});
            skLineSegment(sketch, "E34.right", {"start": v(-40, -300) * mm, "end": v(-40, -340) * mm});
            skSolve(sketch);
        }
        {
            var Q0;
            Q0=makeQuery(id+"F32.imprint","IMPRINT",FACE,{"disambiguationData":[TD([[makeQuery(id+"F32.imprint","IMPRINT",EDGE,{"derivedFrom":sQuery(id+"F32.wireOp",EDGE,"E34.bottom")}),1.0]])]});
            extrude(context, id + "F33", {"entities" : qUnion([Q0]), "operationType" : NewBodyOperationType.ADD, "depth" : 300 * mm});
        }
        {
            var Q0;
            {var subQ1=sQuery(id+"F0.wireOp",EDGE,"E0.bottom");var subQ3=sQuery(id+"F20.wireOp",EDGE,"E20.right");var subQ5=makeQuery(id+"F9.opExtrude","SWEPT_FACE",FACE,{"disambiguationData":[OSD([sQuery(id+"F8.wireOp",EDGE,"E9.left")])]});var subQ6=makeQuery(id+"F21.opExtrude","SWEPT_FACE",FACE,{"disambiguationData":[OSD([subQ3])]});Q0=makeQuery(id+"F24.boolean.opBoolean","SPLIT",FACE,{"disambiguationData":[TD([makeQuery(id+"F1.opExtrude","SWEPT_FACE",FACE,{"disambiguationData":[OSD([subQ1])]})])],"derivedFrom":makeQuery(id+"F21.boolean.opBoolean","MERGE",FACE,{"derivedFrom":[subQ5,subQ6]})});}
            var sketch = newSketch(context, id + "F34", { "sketchPlane" : qUnion([Q0])});
            skLineSegment(sketch, "E35", {"start": v(0, 40) * mm, "end": v(150, 40) * mm});
            skLineSegment(sketch, "E36", {"start": v(150, 35) * mm, "end": v(135, 35) * mm});
            skLineSegment(sketch, "E37.bottom", {"start": v(135, 35) * mm, "end": v(165, 35) * mm});
            skLineSegment(sketch, "E37.top", {"start": v(135, 5) * mm, "end": v(165, 5) * mm});
            skLineSegment(sketch, "E37.left", {"start": v(135, 35) * mm, "end": v(135, 5) * mm});
            skLineSegment(sketch, "E37.right", {"start": v(165, 35) * mm, "end": v(165, 5) * mm});
            skLineSegment(sketch, "E38.bottom", {"start": v(162, 32) * mm, "end": v(138, 32) * mm});
            skLineSegment(sketch, "E38.top", {"start": v(162, 8) * mm, "end": v(138, 8) * mm});
            skLineSegment(sketch, "E38.left", {"start": v(162, 32) * mm, "end": v(162, 8) * mm});
            skLineSegment(sketch, "E38.right", {"start": v(138, 32) * mm, "end": v(138, 8) * mm});
            skSolve(sketch);
        }
        {
            var Q0;
            Q0 = qSketchRegion(id + "F34", true);
            extrude(context, id + "F35", {"entities" : qUnion([Q0]), "operationType" : NewBodyOperationType.ADD, "depth" : 300 * mm});
        }
    });
